FCSTD DOCUMENT  (FreeCAD 0.17R12871 (Git))
Label: Test All - SheetProperties 
License: All rights reserved
LicenseURL: http://en.wikipedia.org/wiki/All_rights_reserved
objects: Spreadsheet::Sheet×23, App::DocumentObjectGroup×4

FEATURE [Spreadsheet::Sheet] Spreadsheet  label="Ungrouped Spreadsheet#1"
FEATURE [Spreadsheet::Sheet] Spreadsheet001  label="Ungrouped Spreadsheet#2"
FEATURE [Spreadsheet::Sheet] Spreadsheet002  label="Headers on 1st Row"
  cells = A1=Units; B1=Alias; C1=Value
FEATURE [Spreadsheet::Sheet] Spreadsheet003  label="Headers on 4th Row"
  cells = B4=Units; C4=Alias; D4=Value
FEATURE [Spreadsheet::Sheet] Spreadsheet004  label="Headers mixed order"
  cells = B4=Alias; C4=Value; D4=Units
FEATURE [Spreadsheet::Sheet] Spreadsheet005  label="Headers Value first"
  cells = B3=Value; C3=Units; D3=Alias
FEATURE [Spreadsheet::Sheet] Spreadsheet006  label="Duplicate Header"
  cells = B2=Alias; C2=Value; D2=Value
FEATURE [Spreadsheet::Sheet] Spreadsheet007  label="First Headers followed by more Headers"
  cells = B3=Alias; C3=Units; D3=Value; J3=Alias
FEATURE [Spreadsheet::Sheet] Spreadsheet008  label="Comments before Headers"
  cells = A1=This is a comment with multiple lines and merged cells:; A2=This is the second line of the comment.; E2=Some text; B4=Alias; C4=Units; D4=Value; A5=1; A6=2; A7=3
FEATURE [Spreadsheet::Sheet] Spreadsheet009  label="Headers Row with Extra Text"
  cells = A1=This is a comment with multiple lines and merged cells:; A2=This is the second line of the comment.; F2=Some text; B4=Description; C4=Alias; D4=Units; E4=Value; A5=1; A6=2; A7=3
FEATURE [Spreadsheet::Sheet] Spreadsheet010  label="Partial Headers"
  cells = A1=Alias; B1=Value
FEATURE [Spreadsheet::Sheet] Spreadsheet011  label="Value Header Missing"
  cells = A1=Alias; B1=Units
FEATURE [Spreadsheet::Sheet] Spreadsheet012  label="Comments including Keywords"
  cells = A1=This is a comment with multiple lines and merged cells:; A2=This is the second line of the comment.; E2=Some text; A3=Some Text Including headers keywords Alias, Units, and Value.; B5=Alias; C5=Units; D5=Value; A6=1; A7=2; A8=3
FEATURE [Spreadsheet::Sheet] Spreadsheet013  label="Headers not on the same Row"
  cells = A1=Alias; B1=Units; C2=Value
FEATURE [App::DocumentObjectGroup] Group001  label="Bad Headers"
  Group = -> [Spreadsheet006,Spreadsheet011,Spreadsheet013]
FEATURE [Spreadsheet::Sheet] Spreadsheet014  label="Headers separated"
  cells = B2=Alias; D2=Units; H2=Value
FEATURE [App::DocumentObjectGroup] Group  label="Good Headers"
  Group = -> [Spreadsheet002,Spreadsheet003,Spreadsheet004,Spreadsheet005,Spreadsheet008,Spreadsheet009,Spreadsheet010,Spreadsheet012,Spreadsheet014,Spreadsheet007]
FEATURE [Spreadsheet::Sheet] Spreadsheet016  label="Full data with comments"
  cells = A1=This is a comment with multiple lines and merged cells:; A2=This is the second line of the comment.; E2=Some text; B4=Alias; C4=Units; D4=Value; A5=1; B5=common_alias_style; C5=mm; D5=3.1400000000000001; A6=2; B6=simpleAlias; C6=cm; D6=700; A7=3; B7=Capital_ALIAS; C7=m; D7=100; A8=4; B8=anotherAlias; C8=in; D8=12; A9=5; B9=YET_ANOTHER_ALIAS; C9=ft; D9=25
FEATURE [Spreadsheet::Sheet] Spreadsheet017  label="Empty rows block in the middle"
  cells = A1=This is a comment with multiple lines and merged cells:; A2=This is the second line of the comment.; E2=Some text; B4=Alias; C4=Units; D4=Value; A5=1; B5=common_alias_style; C5=mm; D5=3.1400000000000001; A6=2; B6=simpleAlias; C6=cm; D6=700; A9=3; B9=Capital_ALIAS; C9=m; D9=100; A10=4; B10=anotherAlias; C10=in; D10=12; A11=5; B11=YET_ANOTHER_ALIAS; C11=ft; D11=25
FEATURE [Spreadsheet::Sheet] Spreadsheet018  label="Multiple empty rows blocks in the middle"
  cells = A1=This is a comment with multiple lines and merged cells:; A2=This is the second line of the comment.; E2=Some text; B4=Alias; C4=Units; D4=Value; A5=1; B5=common_alias_style; C5=mm; D5=3.1400000000000001; A8=2; B8=simpleAlias; C8=cm; D8=700; A9=3; B9=Capital_ALIAS; C9=m; D9=100; A11=4; B11=anotherAlias; C11=in; D11=12; A12=5; B12=YET_ANOTHER_ALIAS; C12=ft; D12=25; A15=6; B15=lastLineAlias; C15=km; D15=2
FEATURE [Spreadsheet::Sheet] Spreadsheet019  label="Empty rows after the header"
  cells = A1=This is a comment with multiple lines and merged cells:; A2=This is the second line of the comment.; E2=Some text; B4=Alias; C4=Units; D4=Value; A7=1; B7=common_alias_style; C7=mm; D7=3.1400000000000001; A8=2; B8=simpleAlias; C8=cm; D8=700; A9=3; B9=Capital_ALIAS; C9=m; D9=100; A10=4; B10=anotherAlias; C10=in; D10=12; A11=5; B11=YET_ANOTHER_ALIAS; C11=ft; D11=25
FEATURE [Spreadsheet::Sheet] Spreadsheet020  label="Invalid units"
  cells = A1=This is a comment with multiple lines and merged cells:; A2=This is the second line of the comment.; E2=Some text; B4=Alias; C4=Units; D4=Value; A5=1; B5=common_alias_style; C5=mm; D5=3.1400000000000001; A6=2; B6=simpleAlias; C6=not_cm; D6=700; A7=3; B7=Capital_ALIAS; C7=m; D7=100; A8=4; B8=anotherAlias; C8=in; D8=12; A9=5; B9=YET_ANOTHER_ALIAS; C9=ft; D9=25
FEATURE [Spreadsheet::Sheet] Spreadsheet021  label="Empty data cells"
  cells = A1=This is a comment with multiple lines and merged cells:; A2=This is the second line of the comment.; E2=Some text; B4=Alias; C4=Units; D4=Value; A5=1; B5=common_alias_style; C5=mm; D5=3.1400000000000001; A6=2; B6=simpleAlias; C6=cm; D6=700; A7=3; C7=m; D7=100; A8=4; B8=anotherAlias; D8=12; A9=5; B9=YET_ANOTHER_ALIAS; C9=ft; D9=25
FEATURE [Spreadsheet::Sheet] Spreadsheet022  label="Comments in the middle"
  cells = A1=This is a comment with multiple lines and merged cells:; A2=This is the second line of the comment.; E2=Some text; B4=Alias; C4=Units; D4=Value; A5=1; B5=common_alias_style; C5=mm; D5=3.1400000000000001; A6=2; B6=simpleAlias; C6=cm; D6=700; A7=3; B7=Capital_ALIAS; C7=m; D7=100; B8=This is a comment in the middle of the data range; A9=4; B9=anotherAlias; C9=in; D9=12; A10=5; B10=YET_ANOTHER_ALIAS; C10=ft; D10=25
FEATURE [App::DocumentObjectGroup] Group002  label="Good Data"
  Group = -> [Spreadsheet016,Spreadsheet017,Spreadsheet018,Spreadsheet019,Spreadsheet021,Spreadsheet022]
FEATURE [Spreadsheet::Sheet] Spreadsheet023  label="Missing Properties Data"
  cells = A1=This is a comment with multiple lines and merged cells:; A2=This is the second line of the comment.; E2=Some text; B4=Alias; C4=Units; D4=Value; A5=1; D5=3.1400000000000001; A6=2; D6=700; A7=3; D7=100; A8=4; D8=12; A9=5; D9=25
FEATURE [App::DocumentObjectGroup] Group003  label="Bad Data"
  Group = -> [Spreadsheet020,Spreadsheet023]
